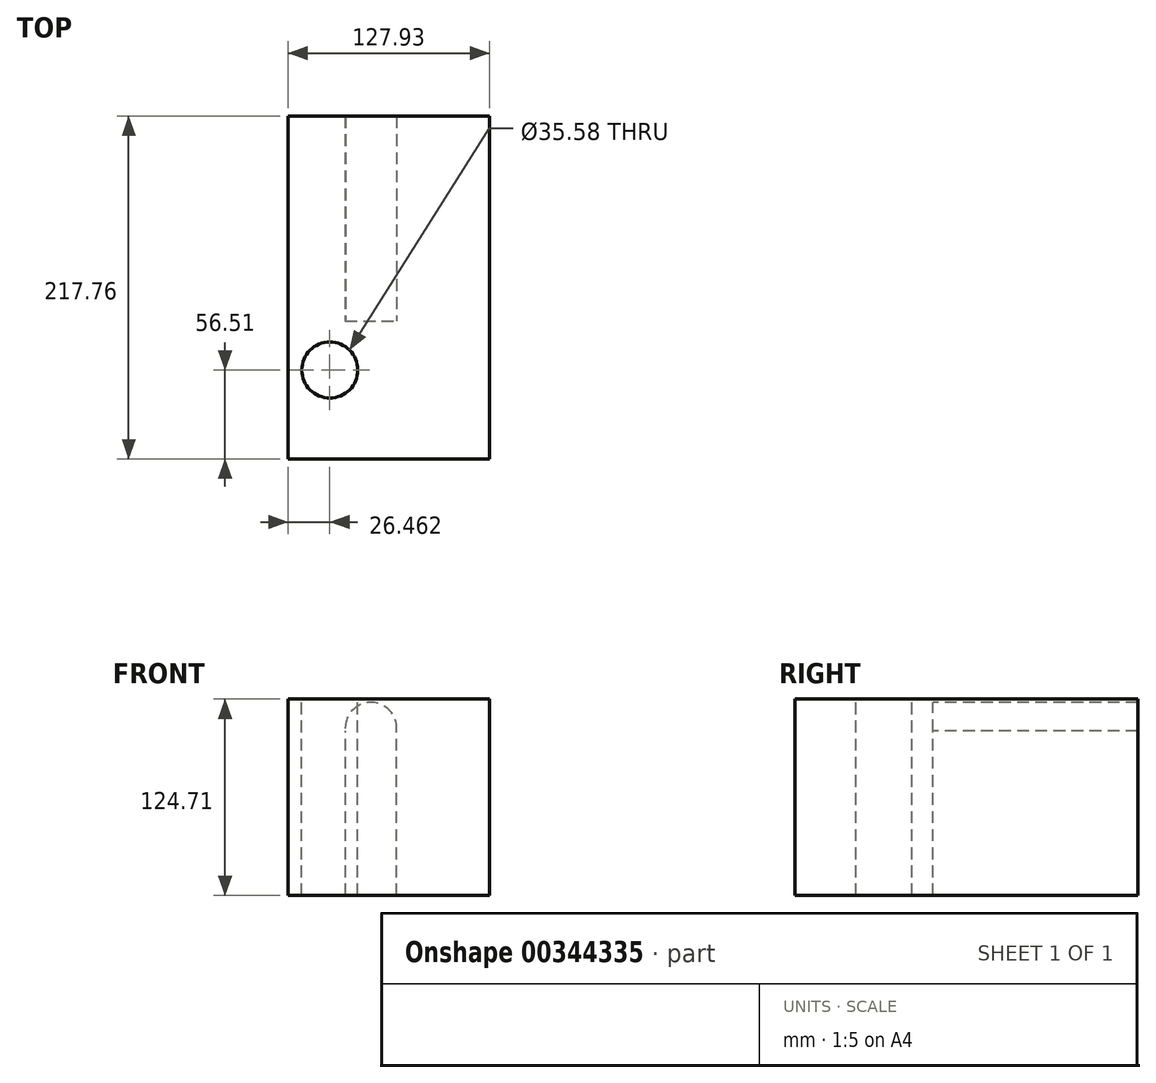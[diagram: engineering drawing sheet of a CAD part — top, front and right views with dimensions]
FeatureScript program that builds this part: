
annotation { "Feature Type Name" : "Feature", "Feature Type Description" : "" }
export const myFeature = defineFeature(function(context is Context, id is Id, definition is map)
    precondition{}
    {
        {
            var Q0;
            Q0=qCreatedBy(makeId("Top.planeOp"),FACE);
            var sketch = newSketch(context, id + "F0", { "sketchPlane" : qUnion([Q0])});
            skLineSegment(sketch, "E0.bottom", {"start": v(-66.88, 31.2) * mm, "end": v(61.05, 31.2) * mm});
            skLineSegment(sketch, "E0.top", {"start": v(-66.88, -56.5) * mm, "end": v(61.05, -56.5) * mm});
            skLineSegment(sketch, "E0.left", {"start": v(-66.88, 31.2) * mm, "end": v(-66.88, -56.5) * mm});
            skLineSegment(sketch, "E0.right", {"start": v(61.05, 31.2) * mm, "end": v(61.05, -56.5) * mm});
            skSolve(sketch);
        }
        {
            var Q0;
            Q0 = qSketchRegion(id + "F0", true);
            extrude(context, id + "F1", {"entities" : qUnion([Q0]), "depth" : 45.72 * mm});
        }
        {
            var Q0;
            Q0=makeQuery(id+"F1.opExtrude","CAP_FACE",FACE,{"disambiguationData":[OSD([sQuery(id+"F0.wireOp",EDGE,"E0.bottom"),sQuery(id+"F0.wireOp",EDGE,"E0.top"),sQuery(id+"F0.wireOp",EDGE,"E0.left"),sQuery(id+"F0.wireOp",EDGE,"E0.right")])],"isStart":false});
            var sketch = newSketch(context, id + "F2", { "sketchPlane" : qUnion([Q0])});
            skCircle(sketch, "E1", {"center": v(-40.42, 0) * mm, "radius": 17.8 * mm});
            skSolve(sketch);
        }
        {
            var Q0;
            Q0=makeQuery(id+"F2.imprint","IMPRINT",FACE,{"disambiguationData":[TD([[makeQuery(id+"F2.imprint","IMPRINT",EDGE,{"derivedFrom":sQuery(id+"F2.wireOp",EDGE,"E1")}),1.0]])]});
            extrude(context, id + "F3", {"entities" : qUnion([Q0]), "operationType" : NewBodyOperationType.REMOVE, "oppositeDirection" : true, "depth" : 45.72 * mm});
        }
        {
            var Q0;
            Q0=makeQuery(id+"F1.opExtrude","SWEPT_FACE",FACE,{"disambiguationData":[OSD([sQuery(id+"F0.wireOp",EDGE,"E0.bottom")])]});
            var sketch = newSketch(context, id + "F4", { "sketchPlane" : qUnion([Q0])});
            skCircle(sketch, "E2", {"center": v(14.23, 27.25) * mm, "radius": 16.36 * mm});
            skPoint(sketch, "E2.first.point", {"position": v(0, 19.18) * mm});
            skPoint(sketch, "E2.second.point", {"position": v(30.48, 25.4) * mm});
            skPoint(sketch, "E2.third.point", {"position": v(19, 11.61) * mm});
            skSolve(sketch);
        }
        {
            var Q0;
            Q0=makeQuery(id+"F4.imprint","IMPRINT",FACE,{"disambiguationData":[TD([[makeQuery(id+"F4.imprint","IMPRINT",EDGE,{"derivedFrom":sQuery(id+"F4.wireOp",EDGE,"E2")}),-1.0]])]});
            extrude(context, id + "F5", {"entities" : qUnion([Q0]), "operationType" : NewBodyOperationType.ADD, "depth" : 130.05 * mm});
        }
        {
            var Q0;
            {var subQ0=sQuery(id+"F0.wireOp",EDGE,"E0.bottom");Q0=makeQuery(id+"F5.boolean.opBoolean","MERGE",FACE,{"derivedFrom":[makeQuery(id+"F1.opExtrude","CAP_FACE",FACE,{"disambiguationData":[OSD([subQ0,sQuery(id+"F0.wireOp",EDGE,"E0.top"),sQuery(id+"F0.wireOp",EDGE,"E0.left"),sQuery(id+"F0.wireOp",EDGE,"E0.right")])],"isStart":true}),makeQuery(id+"F5.opExtrude","SWEPT_FACE",FACE,{"disambiguationData":[OSD([subQ0]),TDD([makeQuery(id+"F4.imprint","IMPRINT",EDGE,{"derivedFrom":makeQuery(id+"F1.opExtrude","CAP_EDGE",EDGE,{"disambiguationData":[OSD([subQ0])],"isStart":true})})])]})]});}
            extrude(context, id + "F6", {"entities" : qUnion([Q0]), "operationType" : NewBodyOperationType.REMOVE, "oppositeDirection" : true, "depth" : 25.4 * mm});
        }
        {
            var Q0;
            Q0=makeQuery(id+"F6.boolean.opBoolean","COPY",FACE,{"derivedFrom":makeQuery(id+"F6.opExtrude","CAP_FACE",FACE,{"disambiguationData":[OSD([sQuery(id+"F0.wireOp",EDGE,"E0.bottom"),sQuery(id+"F0.wireOp",EDGE,"E0.top"),sQuery(id+"F0.wireOp",EDGE,"E0.left"),sQuery(id+"F0.wireOp",EDGE,"E0.right")])],"isStart":false})});
            extrude(context, id + "F7", {"entities" : qUnion([Q0]), "operationType" : NewBodyOperationType.ADD, "depth" : 104.4 * mm});
        }
    });
